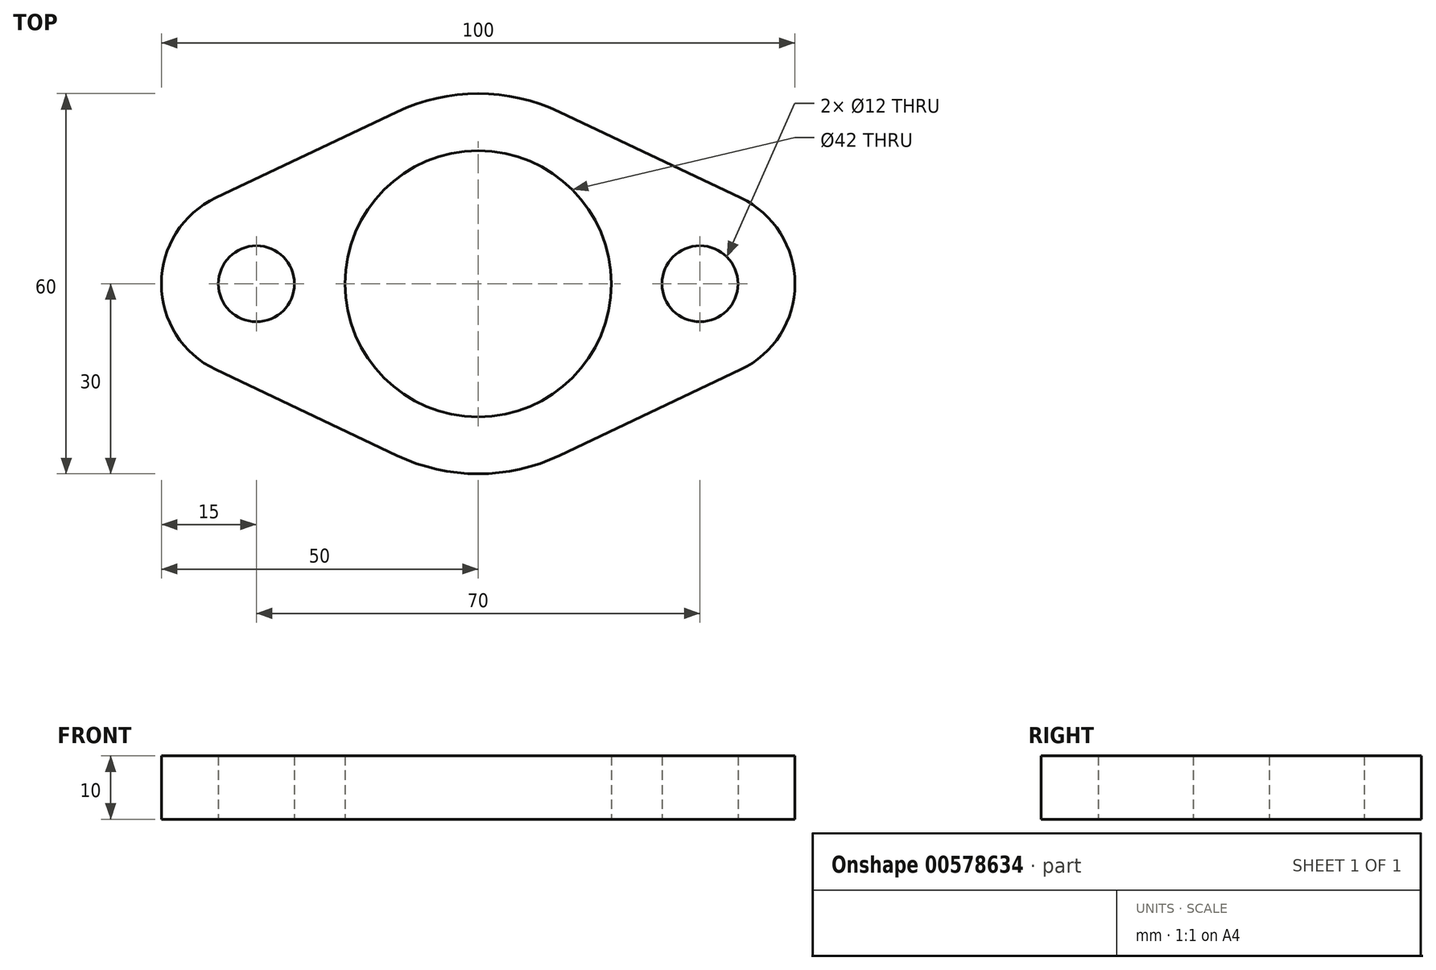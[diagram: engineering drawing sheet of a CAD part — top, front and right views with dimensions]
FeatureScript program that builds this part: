
annotation { "Feature Type Name" : "Feature", "Feature Type Description" : "" }
export const myFeature = defineFeature(function(context is Context, id is Id, definition is map)
    precondition{}
    {
        {
            var Q0;
            Q0=qCreatedBy(makeId("Top.planeOp"),FACE);
            var sketch = newSketch(context, id + "F0", { "sketchPlane" : qUnion([Q0])});
            skArc(sketch, "E0", {"start": v(-12.86, -27.1) * mm, "mid": v(0, -30) * mm, "end": v(12.86, -27.1) * mm});
            skCircle(sketch, "E1", {"center": v(0, 0) * mm, "radius": 21 * mm});
            skCircle(sketch, "E2", {"center": v(-35, 0) * mm, "radius": 6 * mm});
            skArc(sketch, "E3", {"start": v(-41.43, 13.55) * mm, "mid": v(-50, 0) * mm, "end": v(-41.43, -13.55) * mm});
            skCircle(sketch, "E4", {"center": v(35, 0) * mm, "radius": 6 * mm});
            skArc(sketch, "E5", {"start": v(41.43, -13.55) * mm, "mid": v(50, 0) * mm, "end": v(41.43, 13.55) * mm});
            skLineSegment(sketch, "E6", {"start": v(-41.43, 13.55) * mm, "end": v(-12.86, 27.1) * mm});
            skLineSegment(sketch, "E7", {"start": v(12.86, 27.1) * mm, "end": v(41.43, 13.55) * mm});
            skLineSegment(sketch, "E8", {"start": v(-41.43, -13.55) * mm, "end": v(-12.86, -27.1) * mm});
            skLineSegment(sketch, "E9.trimOffspring", {"start": v(12.86, -27.1) * mm, "end": v(41.43, -13.55) * mm});
            skArc(sketch, "E10.trimOffspring", {"start": v(12.86, 27.1) * mm, "mid": v(0, 30) * mm, "end": v(-12.86, 27.1) * mm});
            skSolve(sketch);
        }
        {
            var Q0;
            Q0=makeQuery(id+"F0.imprint","IMPRINT",FACE,{"disambiguationData":[TD([[makeQuery(id+"F0.imprint","IMPRINT",EDGE,{"derivedFrom":sQuery(id+"F0.wireOp",EDGE,"E0")}),1.0]])]});
            extrude(context, id + "F1", {"entities" : qUnion([Q0]), "depth" : 10 * mm, "offsetDistance" : 25 * mm});
        }
    });
